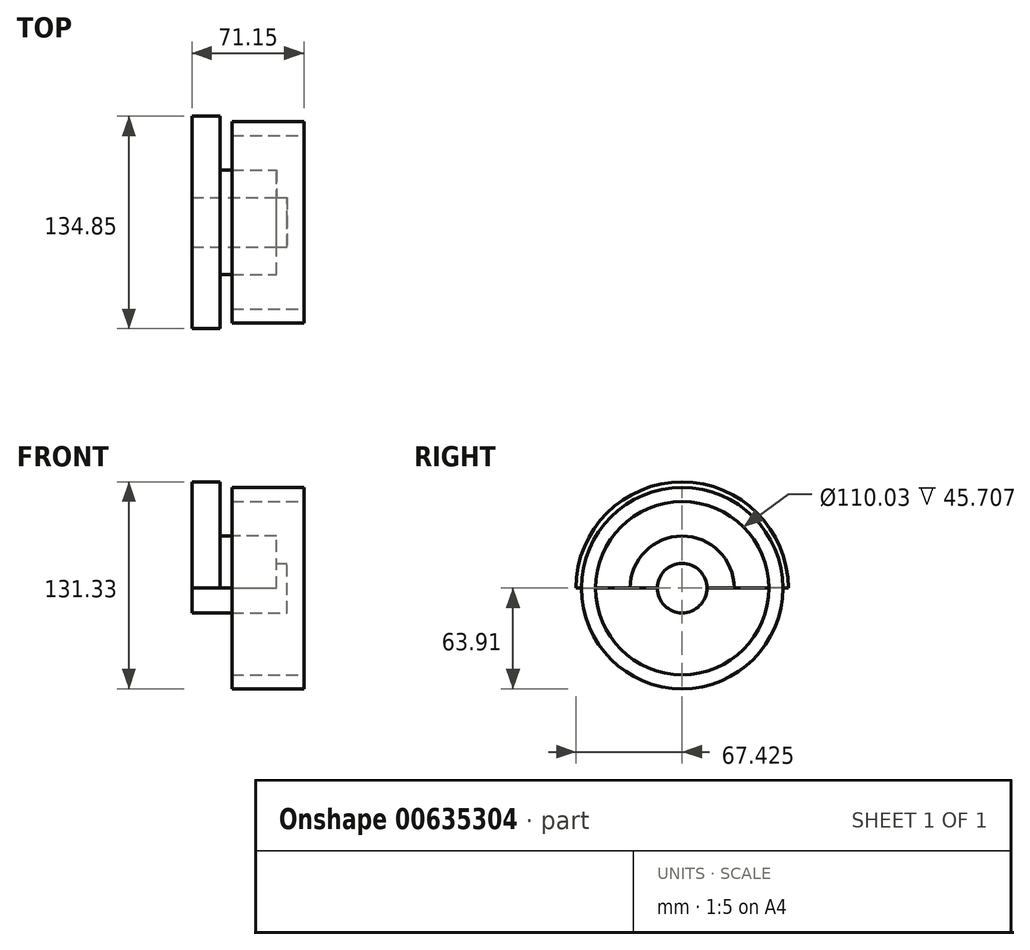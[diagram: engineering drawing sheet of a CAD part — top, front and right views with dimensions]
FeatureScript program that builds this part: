
annotation { "Feature Type Name" : "Feature", "Feature Type Description" : "" }
export const myFeature = defineFeature(function(context is Context, id is Id, definition is map)
    precondition{}
    {
        {
            var Q0;
            Q0=qCreatedBy(makeId("Top.planeOp"),FACE);
            var sketch = newSketch(context, id + "F0", { "sketchPlane" : qUnion([Q0])});
            skLineSegment(sketch, "E0.bottom", {"start": v(-24.54, 3.83) * mm, "end": v(-124.54, 3.83) * mm});
            skLineSegment(sketch, "E0.top", {"start": v(-24.54, 43.83) * mm, "end": v(-124.54, 43.83) * mm});
            skLineSegment(sketch, "E0.left", {"start": v(-24.54, 3.83) * mm, "end": v(-24.54, 43.83) * mm});
            skLineSegment(sketch, "E0.right", {"start": v(-124.54, 3.83) * mm, "end": v(-124.54, 43.83) * mm});
            skPoint(sketch, "E0.middle", {"position": v(-74.54, 23.83) * mm});
            skLineSegment(sketch, "E1.bottom", {"start": v(-110.27, -61.55) * mm, "end": v(-160.27, -61.55) * mm});
            skLineSegment(sketch, "E1.top", {"start": v(-110.27, -31.55) * mm, "end": v(-160.27, -31.55) * mm});
            skLineSegment(sketch, "E1.left", {"start": v(-110.27, -61.55) * mm, "end": v(-110.27, -31.55) * mm});
            skLineSegment(sketch, "E1.right", {"start": v(-160.27, -61.55) * mm, "end": v(-160.27, -31.55) * mm});
            skPoint(sketch, "E1.middle", {"position": v(-135.27, -46.55) * mm});
            skLineSegment(sketch, "E2", {"start": v(17.4, -52.62) * mm, "end": v(67.4, -52.62) * mm});
            skLineSegment(sketch, "E3", {"start": v(67.4, -52.62) * mm, "end": v(67.4, -31.27) * mm});
            skLineSegment(sketch, "E4", {"start": v(67.4, -31.27) * mm, "end": v(49.33, -31.27) * mm});
            skLineSegment(sketch, "E5", {"start": v(49.33, -31.27) * mm, "end": v(49.33, -18.54) * mm});
            skLineSegment(sketch, "E6", {"start": v(42.28, -11.5) * mm, "end": v(27.64, -11.5) * mm});
            skLineSegment(sketch, "E7", {"start": v(27.64, -11.5) * mm, "end": v(27.64, -6.5) * mm});
            skLineSegment(sketch, "E8", {"start": v(24.64, -3.5) * mm, "end": v(17.4, -3.5) * mm});
            skLineSegment(sketch, "E9", {"start": v(17.4, -3.5) * mm, "end": v(17.4, -52.62) * mm});
            skLineSegment(sketch, "E10", {"start": v(-24.54, 43.83) * mm, "end": v(-9.18, 16.4) * mm});
            skLineSegment(sketch, "E11", {"start": v(-15.48, -10.66) * mm, "end": v(-24.54, -16.9) * mm});
            skLineSegment(sketch, "E12", {"start": v(-24.54, -16.9) * mm, "end": v(-24.54, 3.83) * mm});
            skLineSegment(sketch, "E13", {"start": v(17.4, 31.57) * mm, "end": v(41.33, 19.45) * mm});
            skLineSegment(sketch, "E14", {"start": v(41.33, 19.45) * mm, "end": v(31.76, 11.16) * mm});
            skPoint(sketch, "E15.visualSharp", {"position": v(0, 0) * mm});
            skArc(sketch, "E15.filletArc", {"start": v(-15.48, -10.66) * mm, "mid": v(-7.1, 1.65) * mm, "end": v(-9.18, 16.4) * mm});
            skPoint(sketch, "E16.visualSharp", {"position": v(49.33, -11.5) * mm});
            skArc(sketch, "E16.filletArc", {"start": v(49.33, -18.54) * mm, "mid": v(47.26, -13.56) * mm, "end": v(42.28, -11.5) * mm});
            skPoint(sketch, "E17.visualSharp", {"position": v(27.64, -3.5) * mm});
            skArc(sketch, "E17.filletArc", {"start": v(27.64, -6.5) * mm, "mid": v(26.76, -4.39) * mm, "end": v(24.64, -3.5) * mm});
            skCircle(sketch, "E18", {"center": v(67.4, -31.27) * mm, "radius": 5.86 * mm});
            skSolve(sketch);
        }
        {
            var Q0;
            Q0=makeQuery(id+"F0.imprint","IMPRINT",FACE,{"disambiguationData":[TD([[makeQuery(id+"F0.imprint","IMPRINT",EDGE,{"derivedFrom":sQuery(id+"F0.wireOp",EDGE,"E0.bottom")}),-1.0]])]});
            var sketch = newSketch(context, id + "F1", { "sketchPlane" : qUnion([Q0])});
            skLineSegment(sketch, "E19.bottom", {"start": v(-5.97, 38.55) * mm, "end": v(12.02, 38.55) * mm});
            skLineSegment(sketch, "E19.top", {"start": v(-5.97, 4.22) * mm, "end": v(12.02, 4.22) * mm});
            skLineSegment(sketch, "E19.left", {"start": v(-5.97, 38.55) * mm, "end": v(-5.97, 4.22) * mm});
            skLineSegment(sketch, "E19.right", {"start": v(12.02, 38.55) * mm, "end": v(12.02, 4.22) * mm});
            skLineSegment(sketch, "E20.bottom", {"start": v(-5.97, 4.22) * mm, "end": v(47.8, 4.22) * mm});
            skLineSegment(sketch, "E20.top", {"start": v(-5.97, -13.16) * mm, "end": v(47.8, -13.16) * mm});
            skLineSegment(sketch, "E20.left", {"start": v(-5.97, 4.22) * mm, "end": v(-5.97, -13.16) * mm});
            skLineSegment(sketch, "E20.right", {"start": v(47.8, 4.22) * mm, "end": v(47.8, -13.16) * mm});
            skLineSegment(sketch, "E21.bottom", {"start": v(19.47, 35.03) * mm, "end": v(65.18, 35.03) * mm});
            skLineSegment(sketch, "E21.top", {"start": v(19.47, 26.14) * mm, "end": v(65.18, 26.14) * mm});
            skLineSegment(sketch, "E21.left", {"start": v(19.47, 35.03) * mm, "end": v(19.47, 26.14) * mm});
            skLineSegment(sketch, "E21.right", {"start": v(65.18, 35.03) * mm, "end": v(65.18, 26.14) * mm});
            skLineSegment(sketch, "E22.bottom", {"start": v(65.18, 26.14) * mm, "end": v(54.42, 26.14) * mm});
            skLineSegment(sketch, "E22.top", {"start": v(65.18, -28.88) * mm, "end": v(54.42, -28.88) * mm});
            skLineSegment(sketch, "E22.left", {"start": v(65.18, 26.14) * mm, "end": v(65.18, -28.88) * mm});
            skLineSegment(sketch, "E22.right", {"start": v(54.42, 26.14) * mm, "end": v(54.42, -28.88) * mm});
            skLineSegment(sketch, "E23.bottom", {"start": v(54.42, -28.88) * mm, "end": v(-5.97, -28.88) * mm});
            skLineSegment(sketch, "E23.top", {"start": v(54.42, -13.16) * mm, "end": v(-5.97, -13.16) * mm});
            skLineSegment(sketch, "E23.left", {"start": v(54.42, -28.88) * mm, "end": v(54.42, -13.16) * mm});
            skLineSegment(sketch, "E23.right", {"start": v(-5.97, -28.88) * mm, "end": v(-5.97, -13.16) * mm});
            skSolve(sketch);
        }
        {
            var Q0;
            {var subQ2=sQuery(id+"F1.wireOp",EDGE,"E20.left");Q0=makeQuery(id+"F1.imprint","IMPRINT",FACE,{"disambiguationData":[TD([[makeQuery(id+"F1.imprint","IMPRINT",EDGE,{"derivedFrom":subQ2}),1.0]])]});}
            var Q1;
            Q1=makeQuery(id+"F1.imprint","IMPRINT",FACE,{"disambiguationData":[TD([[makeQuery(id+"F1.imprint","IMPRINT",EDGE,{"derivedFrom":sQuery(id+"F1.wireOp",EDGE,"E19.bottom")}),-1.0]])]});
            var Q2;
            Q2=sQuery(id+"F1.wireOp",EDGE,"E23.bottom");
            revolve(context, id + "F2", {"entities" : qUnion([Q0, Q1]), "axis" : qUnion([Q2]), "revolveType" : RevolveType.ONE_DIRECTION, "oppositeDirection" : true, "angle" : 180 * degree});
        }
        {
            var Q0;
            Q0=makeQuery(id+"F1.imprint","IMPRINT",FACE,{"disambiguationData":[TD([[makeQuery(id+"F1.imprint","IMPRINT",EDGE,{"derivedFrom":sQuery(id+"F1.wireOp",EDGE,"E22.bottom")}),1.0]])]});
            var Q1;
            Q1=makeQuery(id+"F1.imprint","IMPRINT",FACE,{"disambiguationData":[TD([[makeQuery(id+"F1.imprint","IMPRINT",EDGE,{"derivedFrom":sQuery(id+"F1.wireOp",EDGE,"E21.bottom")}),-1.0]])]});
            var Q2;
            Q2=makeQuery(id+"F1.imprint","IMPRINT",FACE,{"disambiguationData":[TD([[makeQuery(id+"F1.imprint","IMPRINT",EDGE,{"derivedFrom":sQuery(id+"F1.wireOp",EDGE,"E23.bottom")}),-1.0]])]});
            var Q3;
            Q3=sQuery(id+"F1.wireOp",EDGE,"E22.top");
            revolve(context, id + "F3", {"operationType" : NewBodyOperationType.ADD, "entities" : qUnion([Q0, Q1, Q2]), "axis" : qUnion([Q3]), "revolveType" : RevolveType.FULL});
        }
    });
